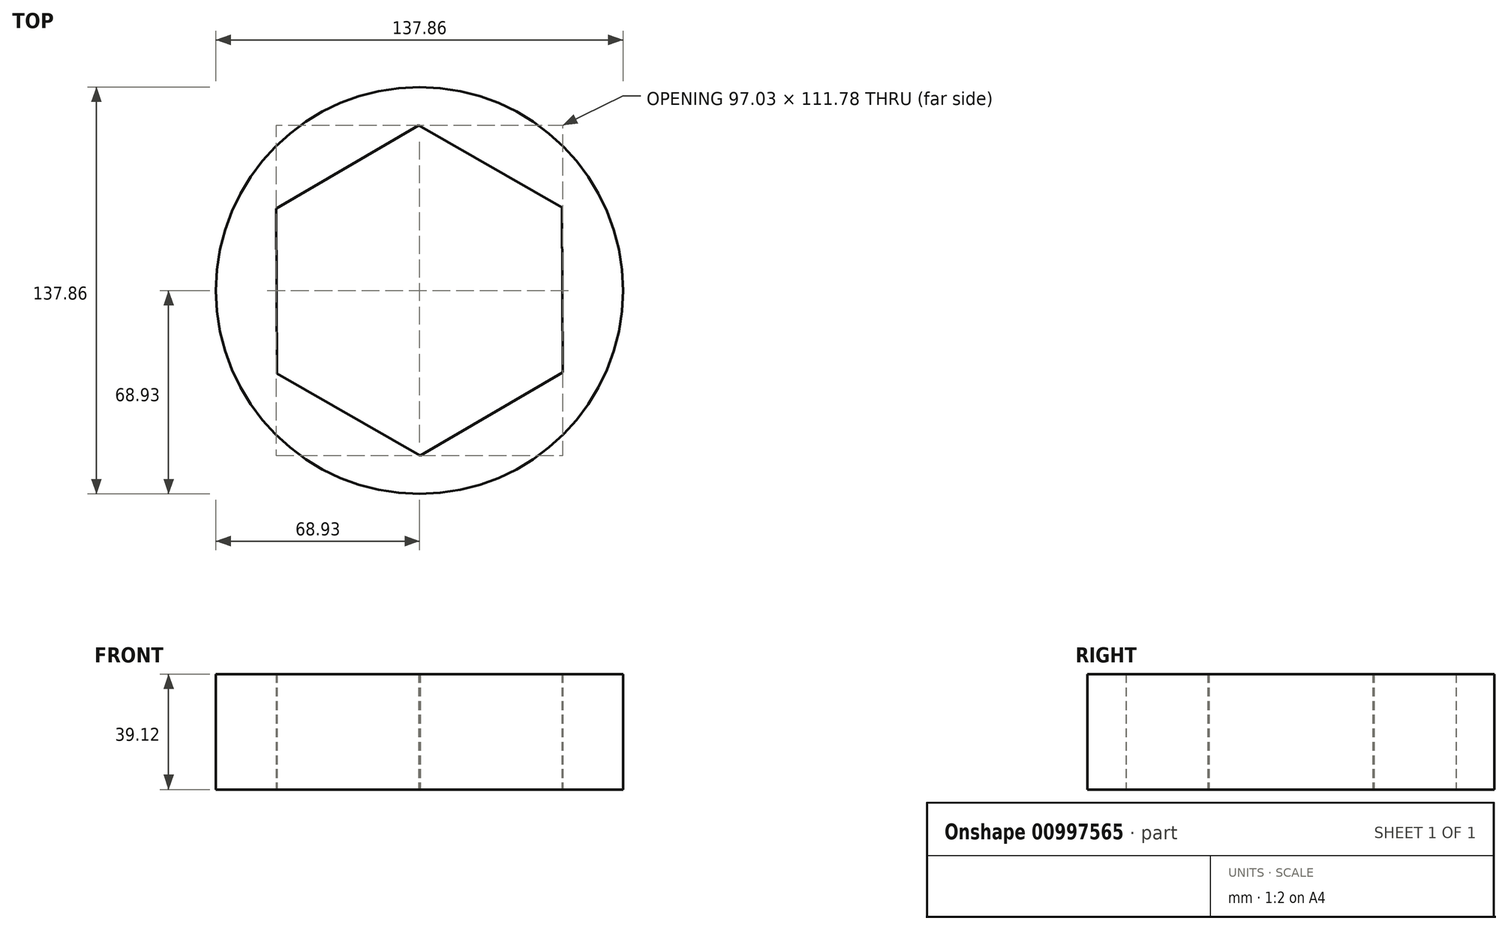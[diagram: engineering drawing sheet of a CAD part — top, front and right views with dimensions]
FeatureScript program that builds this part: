
annotation { "Feature Type Name" : "Feature", "Feature Type Description" : "" }
export const myFeature = defineFeature(function(context is Context, id is Id, definition is map)
    precondition{}
    {
        {
            var Q0;
            Q0=qCreatedBy(makeId("Top.planeOp"),FACE);
            var sketch = newSketch(context, id + "F0", { "sketchPlane" : qUnion([Q0])});
            skCircle(sketch, "E0", {"center": v(0, 0) * mm, "radius": 68.93 * mm});
            skSolve(sketch);
        }
        {
            var Q0;
            Q0=makeQuery(id+"F0.imprint","IMPRINT",FACE,{"disambiguationData":[TD([[makeQuery(id+"F0.imprint","IMPRINT",EDGE,{"derivedFrom":sQuery(id+"F0.wireOp",EDGE,"E0")}),1.0]])]});
            extrude(context, id + "F1", {"entities" : qUnion([Q0]), "depth" : 39.12 * mm, "offsetDistance" : 25.4 * mm});
        }
        {
            var Q0;
            Q0=qCreatedBy(makeId("Top.planeOp"),FACE);
            var sketch = newSketch(context, id + "F2", { "sketchPlane" : qUnion([Q0])});
            skCircle(sketch, "E1.cCircle", {"center": v(0, 0) * mm, "radius": 55.9 * mm, "construction": true});
            skLineSegment(sketch, "E1.0", {"start": v(-48.52, 27.75) * mm, "end": v(-0.23, 55.9) * mm});
            skLineSegment(sketch, "E1.1", {"start": v(-0.23, 55.9) * mm, "end": v(48.29, 28.14) * mm});
            skLineSegment(sketch, "E1.2", {"start": v(48.29, 28.14) * mm, "end": v(48.52, -27.75) * mm});
            skLineSegment(sketch, "E1.3", {"start": v(48.52, -27.75) * mm, "end": v(0.23, -55.9) * mm});
            skLineSegment(sketch, "E1.4", {"start": v(0.23, -55.9) * mm, "end": v(-48.29, -28.14) * mm});
            skLineSegment(sketch, "E1.5", {"start": v(-48.29, -28.14) * mm, "end": v(-48.52, 27.75) * mm});
            skSolve(sketch);
        }
        {
            var Q0;
            Q0 = qSketchRegion(id + "F2", true);
            extrude(context, id + "F3", {"entities" : qUnion([Q0]), "operationType" : NewBodyOperationType.REMOVE, "endBound" : BoundingType.THROUGH_ALL, "depth" : 25.4 * mm, "offsetDistance" : 25.4 * mm});
        }
    });
